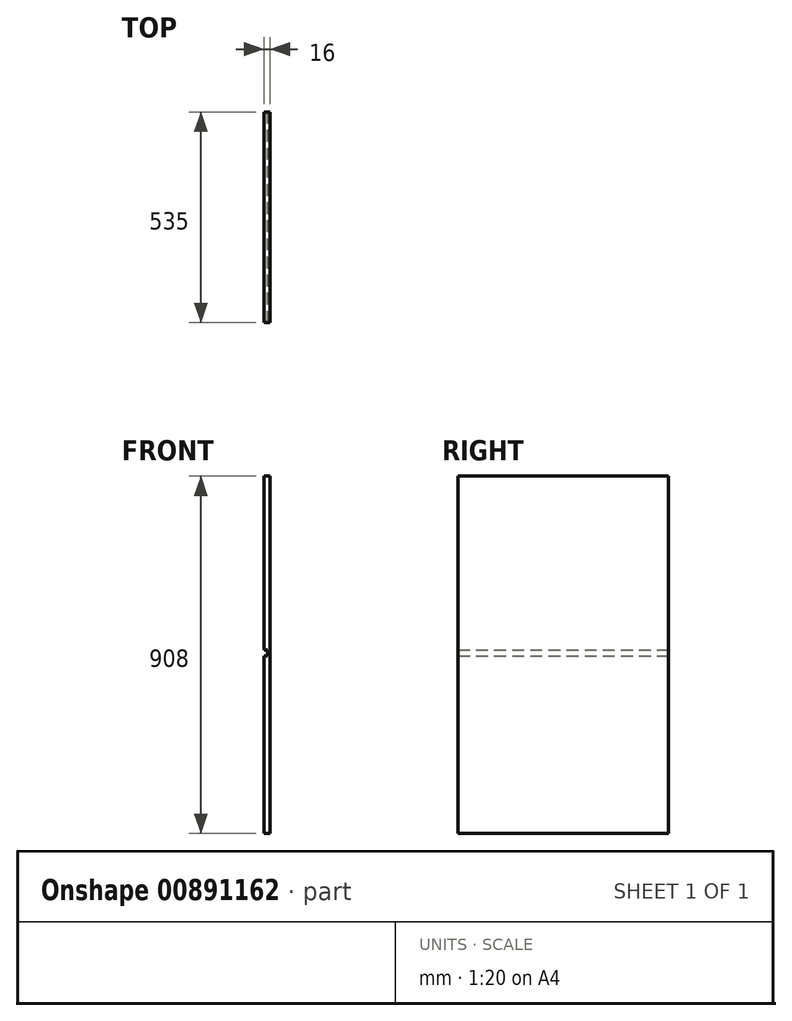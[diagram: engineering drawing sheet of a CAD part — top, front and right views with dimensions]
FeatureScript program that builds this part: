
annotation { "Feature Type Name" : "Feature", "Feature Type Description" : "" }
export const myFeature = defineFeature(function(context is Context, id is Id, definition is map)
    precondition{}
    {
        {
            var Q0;
            Q0=qCreatedBy(makeId("Right.planeOp"),FACE);
            var sketch = newSketch(context, id + "F0", { "sketchPlane" : qUnion([Q0])});
            skLineSegment(sketch, "E0.bottom", {"start": v(-277.43, 620.24) * mm, "end": v(257.57, 620.24) * mm});
            skLineSegment(sketch, "E0.top", {"start": v(-277.43, -287.76) * mm, "end": v(257.57, -287.76) * mm});
            skLineSegment(sketch, "E0.left", {"start": v(-277.43, 620.24) * mm, "end": v(-277.43, -287.76) * mm});
            skLineSegment(sketch, "E0.right", {"start": v(257.57, 620.24) * mm, "end": v(257.57, -287.76) * mm});
            skLineSegment(sketch, "E1", {"start": v(-277.43, 163.24) * mm, "end": v(257.57, 163.24) * mm});
            skLineSegment(sketch, "E2", {"start": v(-277.43, 179.24) * mm, "end": v(257.57, 179.24) * mm});
            skLineSegment(sketch, "E3", {"start": v(-277.43, -271.76) * mm, "end": v(257.57, -271.76) * mm});
            skSolve(sketch);
        }
        {
            var Q0;
            Q0 = qSketchRegion(id + "F0", true);
            extrude(context, id + "F1", {"entities" : qUnion([Q0]), "depth" : 16 * mm, "offsetDistance" : 25 * mm});
        }
        {
            var Q0;
            {var subQ0=sQuery(id+"F0.wireOp",EDGE,"E1");Q0=makeQuery(id+"F0.imprint","IMPRINT",FACE,{"disambiguationData":[TD([[makeQuery(id+"F0.imprint","IMPRINT",EDGE,{"derivedFrom":subQ0}),1.0]])]});}
            extrude(context, id + "F2", {"entities" : qUnion([Q0]), "operationType" : NewBodyOperationType.REMOVE, "depth" : 10 * mm, "offsetDistance" : 25 * mm});
        }
    });
